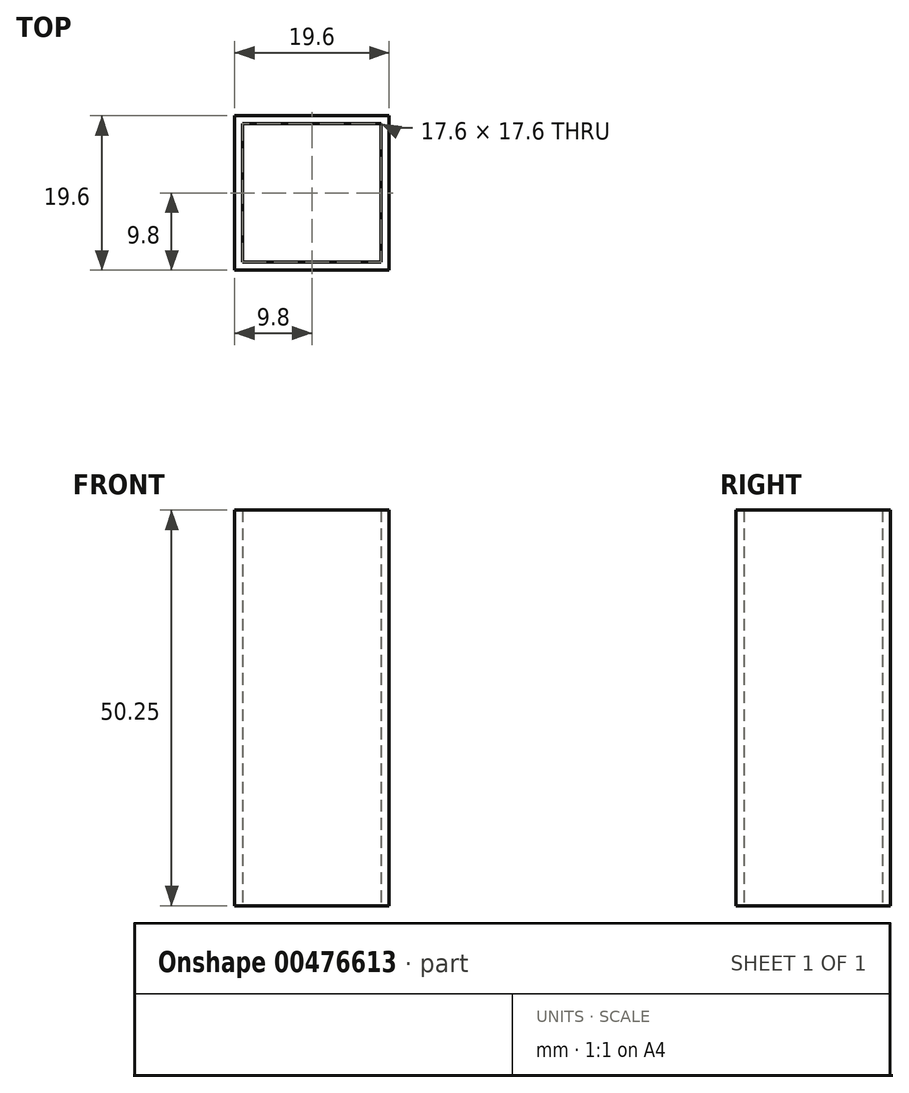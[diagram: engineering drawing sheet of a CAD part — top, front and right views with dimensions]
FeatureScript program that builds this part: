
annotation { "Feature Type Name" : "Feature", "Feature Type Description" : "" }
export const myFeature = defineFeature(function(context is Context, id is Id, definition is map)
    precondition{}
    {
        {
            var Q0;
            Q0=qCreatedBy(makeId("Top.planeOp"),FACE);
            var sketch = newSketch(context, id + "F0", { "sketchPlane" : qUnion([Q0])});
            skLineSegment(sketch, "E0.bottom", {"start": v(9.8, 9.8) * mm, "end": v(-9.8, 9.8) * mm});
            skLineSegment(sketch, "E0.top", {"start": v(9.8, -9.8) * mm, "end": v(-9.8, -9.8) * mm});
            skLineSegment(sketch, "E0.left", {"start": v(9.8, 9.8) * mm, "end": v(9.8, -9.8) * mm});
            skLineSegment(sketch, "E0.right", {"start": v(-9.8, 9.8) * mm, "end": v(-9.8, -9.8) * mm});
            skPoint(sketch, "E0.middle", {"position": v(0, 0) * mm});
            skLineSegment(sketch, "E1.bottom", {"start": v(8.8, 8.8) * mm, "end": v(-8.8, 8.8) * mm});
            skLineSegment(sketch, "E1.top", {"start": v(8.8, -8.8) * mm, "end": v(-8.8, -8.8) * mm});
            skLineSegment(sketch, "E1.left", {"start": v(8.8, 8.8) * mm, "end": v(8.8, -8.8) * mm});
            skLineSegment(sketch, "E1.right", {"start": v(-8.8, 8.8) * mm, "end": v(-8.8, -8.8) * mm});
            skSolve(sketch);
        }
        {
            var Q0;
            Q0 = qSketchRegion(id + "F0", true);
            extrude(context, id + "F1", {"entities" : qUnion([Q0]), "depth" : 50.25 * mm});
        }
    });
